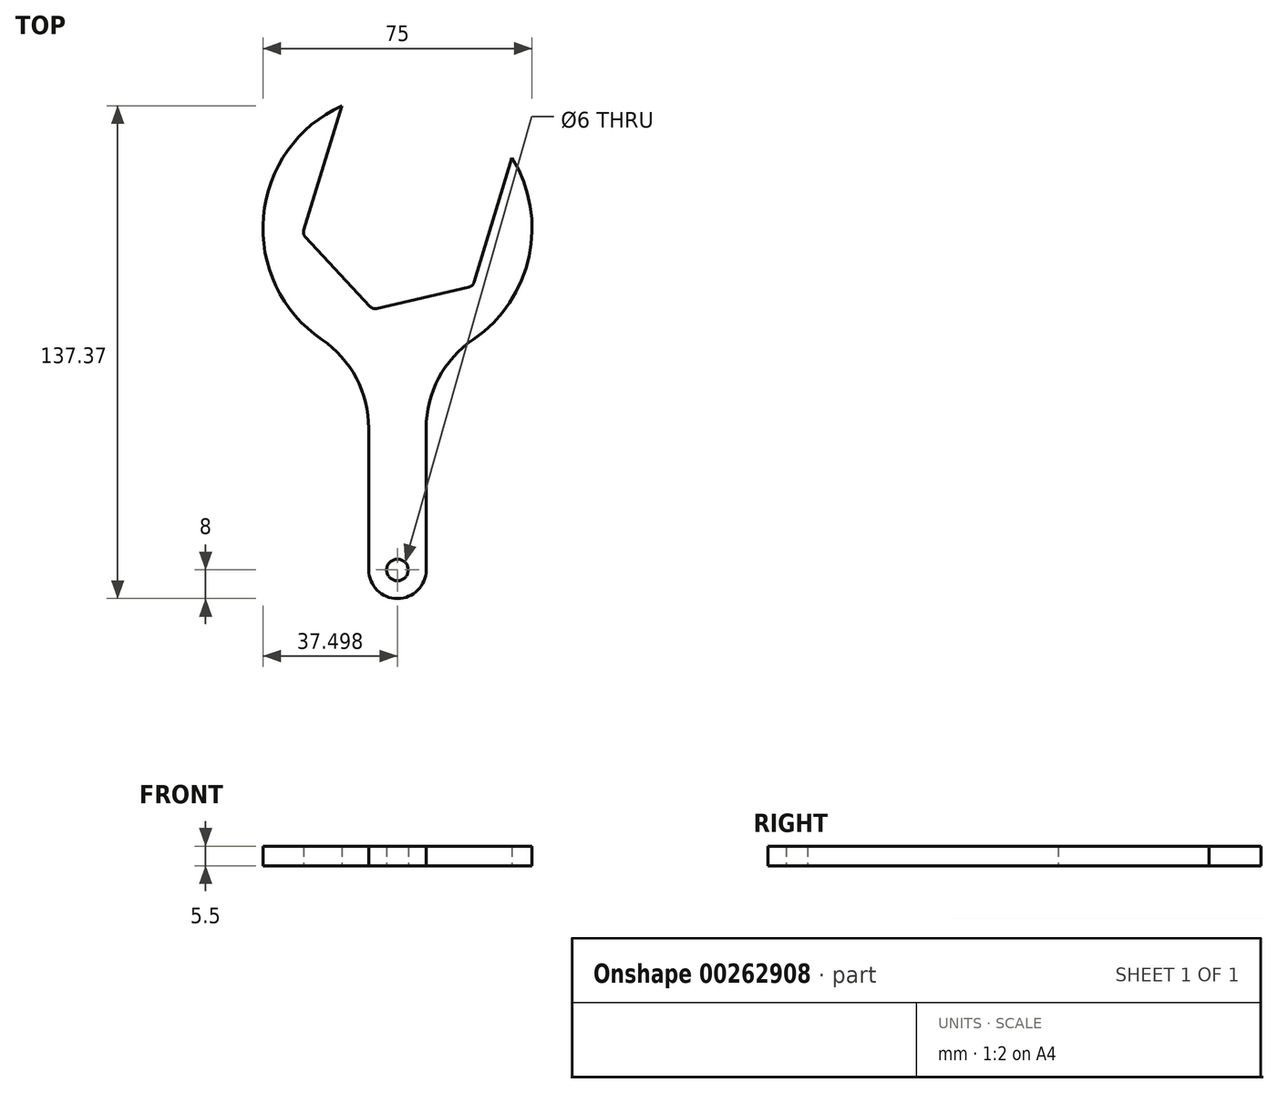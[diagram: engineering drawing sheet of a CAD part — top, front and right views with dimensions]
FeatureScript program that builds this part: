
annotation { "Feature Type Name" : "Feature", "Feature Type Description" : "" }
export const myFeature = defineFeature(function(context is Context, id is Id, definition is map)
    precondition{}
    {
        {
            var Q0;
            Q0=qCreatedBy(makeId("Top.planeOp"),FACE);
            var sketch = newSketch(context, id + "F0", { "sketchPlane" : qUnion([Q0])});
            skCircle(sketch, "E0.cCircle", {"center": v(0, 0) * mm, "radius": 24.8 * mm, "construction": true});
            skLineSegment(sketch, "E0.0", {"start": v(30.48, 14.87) * mm, "end": v(19.87, -19.84) * mm});
            skLineSegment(sketch, "E0.1", {"start": v(18.4, -21.2) * mm, "end": v(-7.25, -27.13) * mm});
            skLineSegment(sketch, "E0.2", {"start": v(-9.16, -26.54) * mm, "end": v(-27.12, -7.29) * mm});
            skLineSegment(sketch, "E0.3", {"start": v(-27.57, -5.34) * mm, "end": v(-16.95, 29.37) * mm});
            skLineSegment(sketch, "E0.4", {"start": v(-19.53, 20.94) * mm, "end": v(8.37, 27.39) * mm, "construction": true});
            skLineSegment(sketch, "E0.5", {"start": v(8.37, 27.39) * mm, "end": v(27.9, 6.44) * mm, "construction": true});
            skPoint(sketch, "E0.0.midPoint", {"position": v(23.72, -7.25) * mm});
            skArc(sketch, "E1", {"start": v(-9.46, -100) * mm, "mid": v(-1.46, -108) * mm, "end": v(6.54, -100) * mm});
            skLineSegment(sketch, "E2.trimOffspring", {"start": v(6.54, -60.57) * mm, "end": v(6.54, -100) * mm});
            skLineSegment(sketch, "E3.trimOffspring", {"start": v(-9.46, -60.57) * mm, "end": v(-9.46, -100) * mm});
            skCircle(sketch, "E4", {"center": v(-1.46, -100) * mm, "radius": 3 * mm});
            skPoint(sketch, "E5.visualSharp", {"position": v(27.9, 6.44) * mm});
            skPoint(sketch, "E6.visualSharp", {"position": v(-19.53, 20.94) * mm});
            skLineSegment(sketch, "E7", {"start": v(-7.25, -23.72) * mm, "end": v(7.25, 23.72) * mm, "construction": true});
            skArc(sketch, "E8", {"start": v(19.65, -35.77) * mm, "mid": v(35.2, -12.62) * mm, "end": v(30.48, 14.87) * mm});
            skArc(sketch, "E9", {"start": v(-9.46, -41.42) * mm, "mid": v(-1.46, -42.28) * mm, "end": v(6.54, -41.42) * mm, "construction": true});
            skLineSegment(sketch, "E10", {"start": v(-1.46, -4.78) * mm, "end": v(-1.46, -100) * mm, "construction": true});
            skLineSegment(sketch, "E11", {"start": v(-16.95, 29.37) * mm, "end": v(-16.95, 29.37) * mm});
            skArc(sketch, "E12", {"start": v(-16.95, 29.37) * mm, "mid": v(-38.82, -1.56) * mm, "end": v(-22.57, -35.77) * mm});
            skArc(sketch, "E13", {"start": v(30.48, 14.87) * mm, "mid": v(9.5, 31.08) * mm, "end": v(-16.95, 29.37) * mm, "construction": true});
            skPoint(sketch, "E14.visualSharp", {"position": v(6.54, -41.42) * mm});
            skArc(sketch, "E14.filletArc", {"start": v(19.65, -35.77) * mm, "mid": v(10.02, -46.55) * mm, "end": v(6.54, -60.57) * mm});
            skPoint(sketch, "E15.visualSharp", {"position": v(-9.46, -41.42) * mm});
            skArc(sketch, "E15.filletArc", {"start": v(-9.46, -60.57) * mm, "mid": v(-12.94, -46.55) * mm, "end": v(-22.57, -35.77) * mm});
            skPoint(sketch, "E16.visualSharp", {"position": v(-27.9, -6.44) * mm});
            skArc(sketch, "E16.filletArc", {"start": v(-27.57, -5.34) * mm, "mid": v(-27.6, -6.37) * mm, "end": v(-27.12, -7.29) * mm});
            skPoint(sketch, "E17.visualSharp", {"position": v(-8.37, -27.39) * mm});
            skArc(sketch, "E17.filletArc", {"start": v(-9.16, -26.54) * mm, "mid": v(-8.28, -27.09) * mm, "end": v(-7.25, -27.13) * mm});
            skPoint(sketch, "E18.visualSharp", {"position": v(19.53, -20.94) * mm});
            skArc(sketch, "E18.filletArc", {"start": v(18.4, -21.2) * mm, "mid": v(19.32, -20.72) * mm, "end": v(19.87, -19.84) * mm});
            skSolve(sketch);
        }
        {
            var Q0;
            Q0=qSketchRegion(id+"F0",true);
            extrude(context, id + "F1", {"entities" : qUnion([Q0]), "depth" : 5.5 * mm});
        }
    });
